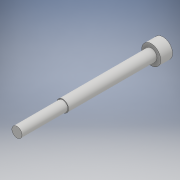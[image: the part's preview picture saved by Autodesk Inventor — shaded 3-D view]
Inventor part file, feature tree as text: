
AUTODESK INVENTOR PART (.ipt)
format: ipt  version: 2018 (Build 220112000, 112)  size: 108,032 bytes
history: native  units: mm
features: extrude x3, sketch x3
ambient origin geometry x8: Origin, YZ Plane, XZ Plane, XY Plane, X Axis, Y Axis, Z Axis, Center Point
bodies: Solid1 (feature_tree)
feature tree (6):
  extrude  "Extrusion1"  Depth=7.92mm TaperAngle=0.0deg
  extrude  "Extrusion2"  Depth=98.1mm TaperAngle=0.0deg
  extrude  "Extrusion3"  Depth=30.75mm TaperAngle=0.0deg
  sketch  "Sketch1"  dims[d0=12.82mm d1=7.92mm d2=0.0mm]
  sketch  "Sketch2"  dims[d3=7.81mm d4=98.1mm d5=0.0mm]
  sketch  "Sketch3"  dims[d6=0.5mm d7=30.75mm d8=0.0mm]
